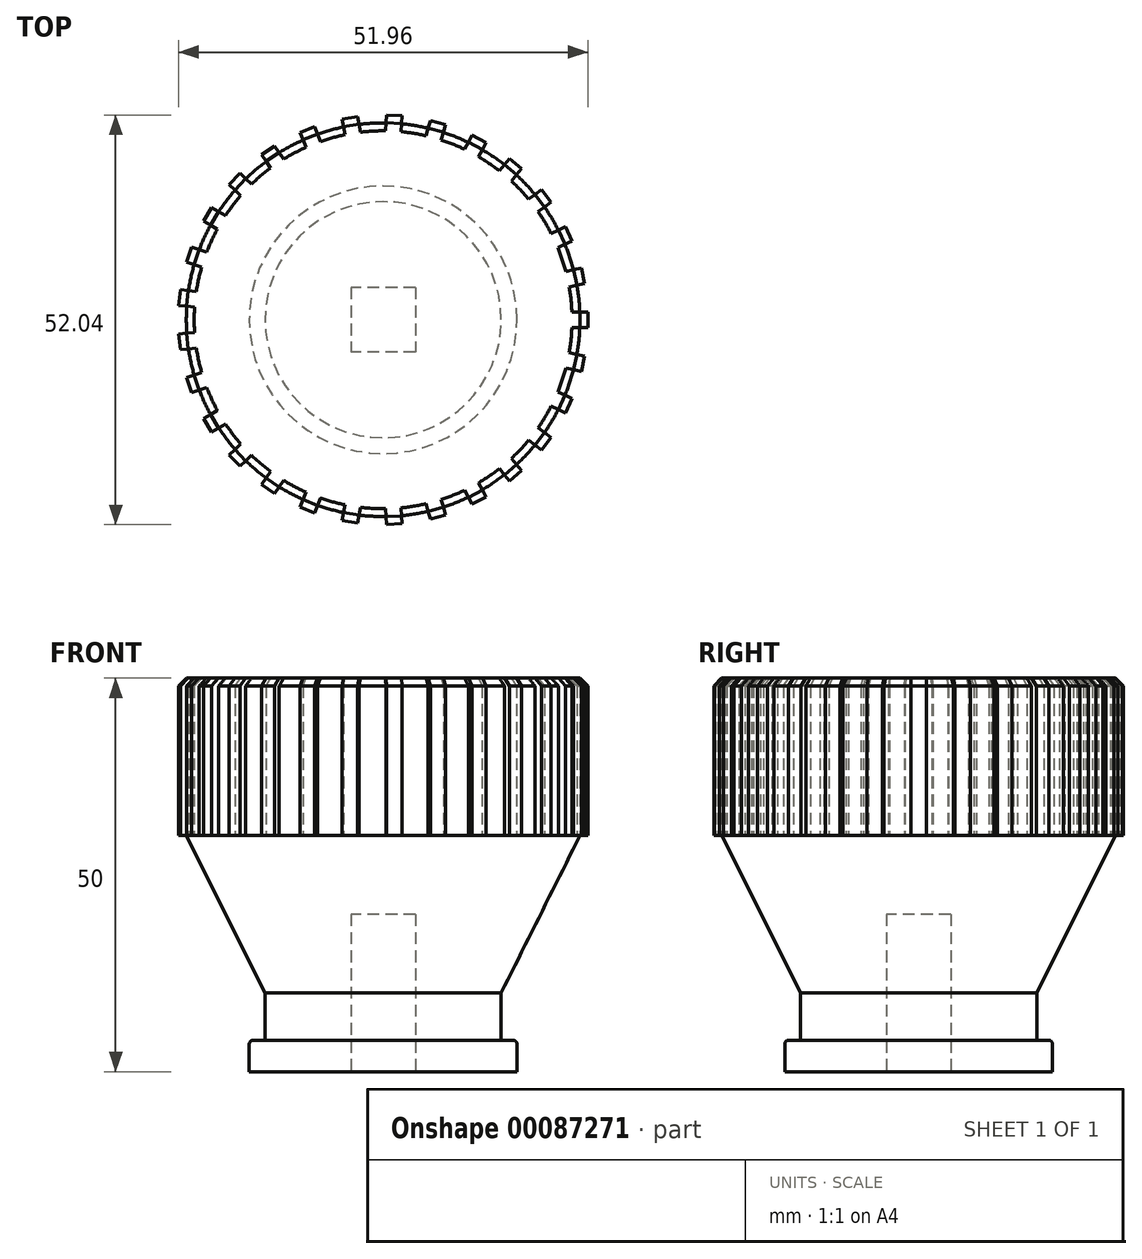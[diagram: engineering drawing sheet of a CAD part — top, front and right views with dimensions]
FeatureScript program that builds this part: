
annotation { "Feature Type Name" : "Feature", "Feature Type Description" : "" }
export const myFeature = defineFeature(function(context is Context, id is Id, definition is map)
    precondition{}
    {
        {
            var Q0;
            Q0=qCreatedBy(makeId("Top.planeOp"),FACE);
            var sketch = newSketch(context, id + "F0", { "sketchPlane" : qUnion([Q0])});
            skCircle(sketch, "E0", {"center": v(0, 0) * mm, "radius": 15 * mm});
            skLineSegment(sketch, "E1", {"start": v(0, 0) * mm, "end": v(0, 4.1) * mm, "construction": true});
            skLineSegment(sketch, "E2", {"start": v(0, 4.1) * mm, "end": v(4.1, 4.1) * mm, "construction": true});
            skLineSegment(sketch, "E3.bottom", {"start": v(4.1, 4.1) * mm, "end": v(-4.1, 4.1) * mm});
            skLineSegment(sketch, "E3.top", {"start": v(4.1, -4.1) * mm, "end": v(-4.1, -4.1) * mm});
            skLineSegment(sketch, "E3.left", {"start": v(4.1, 4.1) * mm, "end": v(4.1, -4.1) * mm});
            skLineSegment(sketch, "E3.right", {"start": v(-4.1, 4.1) * mm, "end": v(-4.1, -4.1) * mm});
            skSolve(sketch);
        }
        {
            var Q0;
            Q0=makeQuery(id+"F0.imprint","IMPRINT",FACE,{"disambiguationData":[TD([[makeQuery(id+"F0.imprint","IMPRINT",EDGE,{"derivedFrom":sQuery(id+"F0.wireOp",EDGE,"E0")}),1.0]])]});
            var Q1;
            Q1=makeQuery(id+"F0.imprint","IMPRINT",FACE,{"disambiguationData":[TD([[makeQuery(id+"F0.imprint","IMPRINT",EDGE,{"derivedFrom":sQuery(id+"F0.wireOp",EDGE,"E3.bottom")}),1.0]])]});
            extrude(context, id + "F1", {"entities" : qUnion([Q0, Q1]), "depth" : 10 * mm});
        }
        {
            var Q0;
            Q0=makeQuery(id+"F1.opExtrude","CAP_FACE",FACE,{"disambiguationData":[OSD([sQuery(id+"F0.wireOp",EDGE,"E0"),sQuery(id+"F0.wireOp",EDGE,"E3.bottom"),sQuery(id+"F0.wireOp",EDGE,"E3.top"),sQuery(id+"F0.wireOp",EDGE,"E3.left"),sQuery(id+"F0.wireOp",EDGE,"E3.right")])],"isStart":false});
            cPlane(context, id + "F2", {"entities" : qUnion([Q0]), "cplaneType" : CPlaneType.OFFSET, "offset" : 20 * mm, "width" : 150 * mm, "height" : 150 * mm});
        }
        {
            var Q0;
            Q0=qCreatedBy(id+"F2.planeOp",FACE);
            var sketch = newSketch(context, id + "F3", { "sketchPlane" : qUnion([Q0])});
            skCircle(sketch, "E4", {"center": v(0, 0) * mm, "radius": 25 * mm});
            skLineSegment(sketch, "E5", {"start": v(26, 0) * mm, "end": v(26, -1) * mm});
            skLineSegment(sketch, "E6", {"start": v(26, 0) * mm, "end": v(26, 1) * mm});
            skLineSegment(sketch, "E7", {"start": v(26, 1) * mm, "end": v(24.98, 1) * mm});
            skLineSegment(sketch, "E8", {"start": v(26, -1) * mm, "end": v(24.98, -1) * mm});
            skLineSegment(sketch, "E9.1.0", {"start": v(25.4, -5.59) * mm, "end": v(25.6, -4.61) * mm});
            skLineSegment(sketch, "E9.1.1", {"start": v(25.4, -5.59) * mm, "end": v(25.18, -6.57) * mm});
            skLineSegment(sketch, "E9.1.2", {"start": v(25.6, -4.61) * mm, "end": v(24.61, -4.4) * mm});
            skLineSegment(sketch, "E9.1.3", {"start": v(25.18, -6.57) * mm, "end": v(24.18, -6.35) * mm});
            skLineSegment(sketch, "E9.2.0", {"start": v(23.6, -10.92) * mm, "end": v(24.02, -10) * mm});
            skLineSegment(sketch, "E9.2.1", {"start": v(23.6, -10.92) * mm, "end": v(23.18, -11.82) * mm});
            skLineSegment(sketch, "E9.2.2", {"start": v(24.02, -10) * mm, "end": v(23.1, -9.58) * mm});
            skLineSegment(sketch, "E9.2.3", {"start": v(23.18, -11.82) * mm, "end": v(22.25, -11.4) * mm});
            skLineSegment(sketch, "E9.3.0", {"start": v(20.7, -15.73) * mm, "end": v(21.3, -14.94) * mm});
            skLineSegment(sketch, "E9.3.1", {"start": v(20.7, -15.73) * mm, "end": v(20.1, -16.53) * mm});
            skLineSegment(sketch, "E9.3.2", {"start": v(21.3, -14.94) * mm, "end": v(20.5, -14.32) * mm});
            skLineSegment(sketch, "E9.3.3", {"start": v(20.1, -16.53) * mm, "end": v(19.28, -15.91) * mm});
            skLineSegment(sketch, "E9.4.0", {"start": v(16.83, -19.82) * mm, "end": v(17.6, -19.17) * mm});
            skLineSegment(sketch, "E9.4.1", {"start": v(16.83, -19.82) * mm, "end": v(16.07, -20.46) * mm});
            skLineSegment(sketch, "E9.4.2", {"start": v(17.6, -19.17) * mm, "end": v(16.93, -18.4) * mm});
            skLineSegment(sketch, "E9.4.3", {"start": v(16.07, -20.46) * mm, "end": v(15.4, -19.69) * mm});
            skLineSegment(sketch, "E9.5.0", {"start": v(12.18, -22.97) * mm, "end": v(13.06, -22.5) * mm});
            skLineSegment(sketch, "E9.5.1", {"start": v(12.18, -22.97) * mm, "end": v(11.3, -23.44) * mm});
            skLineSegment(sketch, "E9.5.2", {"start": v(13.06, -22.5) * mm, "end": v(12.58, -21.6) * mm});
            skLineSegment(sketch, "E9.5.3", {"start": v(11.3, -23.44) * mm, "end": v(10.82, -22.54) * mm});
            skLineSegment(sketch, "E9.6.0", {"start": v(6.96, -25.05) * mm, "end": v(7.92, -24.78) * mm});
            skLineSegment(sketch, "E9.6.1", {"start": v(6.96, -25.05) * mm, "end": v(6, -25.32) * mm});
            skLineSegment(sketch, "E9.6.2", {"start": v(7.92, -24.78) * mm, "end": v(7.65, -23.8) * mm});
            skLineSegment(sketch, "E9.6.3", {"start": v(6, -25.32) * mm, "end": v(5.72, -24.34) * mm});
            skLineSegment(sketch, "E9.7.0", {"start": v(1.4, -25.96) * mm, "end": v(2.4, -25.9) * mm});
            skLineSegment(sketch, "E9.7.1", {"start": v(1.4, -25.96) * mm, "end": v(0.4, -26.02) * mm});
            skLineSegment(sketch, "E9.7.2", {"start": v(2.4, -25.9) * mm, "end": v(2.35, -24.89) * mm});
            skLineSegment(sketch, "E9.7.3", {"start": v(0.4, -26.02) * mm, "end": v(0.35, -25) * mm});
            skLineSegment(sketch, "E9.8.0", {"start": v(-4.2, -25.66) * mm, "end": v(-3.22, -25.82) * mm});
            skLineSegment(sketch, "E9.8.1", {"start": v(-4.2, -25.66) * mm, "end": v(-5.2, -25.5) * mm});
            skLineSegment(sketch, "E9.8.2", {"start": v(-3.22, -25.82) * mm, "end": v(-3.05, -24.81) * mm});
            skLineSegment(sketch, "E9.8.3", {"start": v(-5.2, -25.5) * mm, "end": v(-5.03, -24.49) * mm});
            skLineSegment(sketch, "E9.9.0", {"start": v(-9.62, -24.15) * mm, "end": v(-8.7, -24.52) * mm});
            skLineSegment(sketch, "E9.9.1", {"start": v(-9.62, -24.15) * mm, "end": v(-10.55, -23.78) * mm});
            skLineSegment(sketch, "E9.9.2", {"start": v(-8.7, -24.52) * mm, "end": v(-8.32, -23.58) * mm});
            skLineSegment(sketch, "E9.9.3", {"start": v(-10.55, -23.78) * mm, "end": v(-10.18, -22.84) * mm});
            skLineSegment(sketch, "E9.10.0", {"start": v(-14.6, -21.52) * mm, "end": v(-13.76, -22.08) * mm});
            skLineSegment(sketch, "E9.10.1", {"start": v(-14.6, -21.52) * mm, "end": v(-15.42, -20.96) * mm});
            skLineSegment(sketch, "E9.10.2", {"start": v(-13.76, -22.08) * mm, "end": v(-13.2, -21.24) * mm});
            skLineSegment(sketch, "E9.10.3", {"start": v(-15.42, -20.96) * mm, "end": v(-14.85, -20.11) * mm});
            skLineSegment(sketch, "E9.11.0", {"start": v(-18.88, -17.88) * mm, "end": v(-18.19, -18.6) * mm});
            skLineSegment(sketch, "E9.11.1", {"start": v(-18.88, -17.88) * mm, "end": v(-19.56, -17.15) * mm});
            skLineSegment(sketch, "E9.11.2", {"start": v(-18.19, -18.6) * mm, "end": v(-17.45, -17.9) * mm});
            skLineSegment(sketch, "E9.11.3", {"start": v(-19.56, -17.15) * mm, "end": v(-18.82, -16.45) * mm});
            skLineSegment(sketch, "E9.12.0", {"start": v(-22.28, -13.4) * mm, "end": v(-21.76, -14.26) * mm});
            skLineSegment(sketch, "E9.12.1", {"start": v(-22.28, -13.4) * mm, "end": v(-22.8, -12.55) * mm});
            skLineSegment(sketch, "E9.12.2", {"start": v(-21.76, -14.26) * mm, "end": v(-20.89, -13.74) * mm});
            skLineSegment(sketch, "E9.12.3", {"start": v(-22.8, -12.55) * mm, "end": v(-21.92, -12.02) * mm});
            skLineSegment(sketch, "E9.13.0", {"start": v(-24.64, -8.3) * mm, "end": v(-24.32, -9.25) * mm});
            skLineSegment(sketch, "E9.13.1", {"start": v(-24.64, -8.3) * mm, "end": v(-24.96, -7.35) * mm});
            skLineSegment(sketch, "E9.13.2", {"start": v(-24.32, -9.25) * mm, "end": v(-23.35, -8.92) * mm});
            skLineSegment(sketch, "E9.13.3", {"start": v(-24.96, -7.35) * mm, "end": v(-24, -7.03) * mm});
            skLineSegment(sketch, "E9.14.0", {"start": v(-25.85, -2.81) * mm, "end": v(-25.74, -3.8) * mm});
            skLineSegment(sketch, "E9.14.1", {"start": v(-25.85, -2.81) * mm, "end": v(-25.96, -1.82) * mm});
            skLineSegment(sketch, "E9.14.2", {"start": v(-25.74, -3.8) * mm, "end": v(-24.73, -3.7) * mm});
            skLineSegment(sketch, "E9.14.3", {"start": v(-25.96, -1.82) * mm, "end": v(-24.94, -1.7) * mm});
            skLineSegment(sketch, "E9.15.0", {"start": v(-25.85, 2.81) * mm, "end": v(-25.96, 1.82) * mm});
            skLineSegment(sketch, "E9.15.1", {"start": v(-25.85, 2.81) * mm, "end": v(-25.74, 3.8) * mm});
            skLineSegment(sketch, "E9.15.2", {"start": v(-25.96, 1.82) * mm, "end": v(-24.94, 1.7) * mm});
            skLineSegment(sketch, "E9.15.3", {"start": v(-25.74, 3.8) * mm, "end": v(-24.73, 3.7) * mm});
            skLineSegment(sketch, "E9.16.0", {"start": v(-24.64, 8.3) * mm, "end": v(-24.96, 7.35) * mm});
            skLineSegment(sketch, "E9.16.1", {"start": v(-24.64, 8.3) * mm, "end": v(-24.32, 9.25) * mm});
            skLineSegment(sketch, "E9.16.2", {"start": v(-24.96, 7.35) * mm, "end": v(-24, 7.03) * mm});
            skLineSegment(sketch, "E9.16.3", {"start": v(-24.32, 9.25) * mm, "end": v(-23.35, 8.92) * mm});
            skLineSegment(sketch, "E9.17.0", {"start": v(-22.28, 13.4) * mm, "end": v(-22.8, 12.55) * mm});
            skLineSegment(sketch, "E9.17.1", {"start": v(-22.28, 13.4) * mm, "end": v(-21.76, 14.26) * mm});
            skLineSegment(sketch, "E9.17.2", {"start": v(-22.8, 12.55) * mm, "end": v(-21.92, 12.02) * mm});
            skLineSegment(sketch, "E9.17.3", {"start": v(-21.76, 14.26) * mm, "end": v(-20.89, 13.74) * mm});
            skLineSegment(sketch, "E9.18.0", {"start": v(-18.88, 17.88) * mm, "end": v(-19.56, 17.15) * mm});
            skLineSegment(sketch, "E9.18.1", {"start": v(-18.88, 17.88) * mm, "end": v(-18.19, 18.6) * mm});
            skLineSegment(sketch, "E9.18.2", {"start": v(-19.56, 17.15) * mm, "end": v(-18.82, 16.45) * mm});
            skLineSegment(sketch, "E9.18.3", {"start": v(-18.19, 18.6) * mm, "end": v(-17.45, 17.9) * mm});
            skLineSegment(sketch, "E9.19.0", {"start": v(-14.6, 21.52) * mm, "end": v(-15.42, 20.96) * mm});
            skLineSegment(sketch, "E9.19.1", {"start": v(-14.6, 21.52) * mm, "end": v(-13.76, 22.08) * mm});
            skLineSegment(sketch, "E9.19.2", {"start": v(-15.42, 20.96) * mm, "end": v(-14.85, 20.11) * mm});
            skLineSegment(sketch, "E9.19.3", {"start": v(-13.76, 22.08) * mm, "end": v(-13.2, 21.24) * mm});
            skLineSegment(sketch, "E9.20.0", {"start": v(-9.62, 24.15) * mm, "end": v(-10.55, 23.78) * mm});
            skLineSegment(sketch, "E9.20.1", {"start": v(-9.62, 24.15) * mm, "end": v(-8.7, 24.52) * mm});
            skLineSegment(sketch, "E9.20.2", {"start": v(-10.55, 23.78) * mm, "end": v(-10.18, 22.84) * mm});
            skLineSegment(sketch, "E9.20.3", {"start": v(-8.7, 24.52) * mm, "end": v(-8.32, 23.58) * mm});
            skLineSegment(sketch, "E9.21.0", {"start": v(-4.2, 25.66) * mm, "end": v(-5.2, 25.5) * mm});
            skLineSegment(sketch, "E9.21.1", {"start": v(-4.2, 25.66) * mm, "end": v(-3.22, 25.82) * mm});
            skLineSegment(sketch, "E9.21.2", {"start": v(-5.2, 25.5) * mm, "end": v(-5.03, 24.49) * mm});
            skLineSegment(sketch, "E9.21.3", {"start": v(-3.22, 25.82) * mm, "end": v(-3.05, 24.81) * mm});
            skLineSegment(sketch, "E9.22.0", {"start": v(1.4, 25.96) * mm, "end": v(0.4, 26.02) * mm});
            skLineSegment(sketch, "E9.22.1", {"start": v(1.4, 25.96) * mm, "end": v(2.4, 25.9) * mm});
            skLineSegment(sketch, "E9.22.2", {"start": v(0.4, 26.02) * mm, "end": v(0.35, 25) * mm});
            skLineSegment(sketch, "E9.22.3", {"start": v(2.4, 25.9) * mm, "end": v(2.35, 24.89) * mm});
            skLineSegment(sketch, "E9.23.0", {"start": v(6.96, 25.05) * mm, "end": v(6, 25.32) * mm});
            skLineSegment(sketch, "E9.23.1", {"start": v(6.96, 25.05) * mm, "end": v(7.92, 24.78) * mm});
            skLineSegment(sketch, "E9.23.2", {"start": v(6, 25.32) * mm, "end": v(5.72, 24.34) * mm});
            skLineSegment(sketch, "E9.23.3", {"start": v(7.92, 24.78) * mm, "end": v(7.65, 23.8) * mm});
            skLineSegment(sketch, "E9.24.0", {"start": v(12.18, 22.97) * mm, "end": v(11.3, 23.44) * mm});
            skLineSegment(sketch, "E9.24.1", {"start": v(12.18, 22.97) * mm, "end": v(13.06, 22.5) * mm});
            skLineSegment(sketch, "E9.24.2", {"start": v(11.3, 23.44) * mm, "end": v(10.82, 22.54) * mm});
            skLineSegment(sketch, "E9.24.3", {"start": v(13.06, 22.5) * mm, "end": v(12.58, 21.6) * mm});
            skLineSegment(sketch, "E9.25.0", {"start": v(16.83, 19.82) * mm, "end": v(16.07, 20.46) * mm});
            skLineSegment(sketch, "E9.25.1", {"start": v(16.83, 19.82) * mm, "end": v(17.6, 19.17) * mm});
            skLineSegment(sketch, "E9.25.2", {"start": v(16.07, 20.46) * mm, "end": v(15.4, 19.69) * mm});
            skLineSegment(sketch, "E9.25.3", {"start": v(17.6, 19.17) * mm, "end": v(16.93, 18.4) * mm});
            skLineSegment(sketch, "E9.26.0", {"start": v(20.7, 15.73) * mm, "end": v(20.1, 16.53) * mm});
            skLineSegment(sketch, "E9.26.1", {"start": v(20.7, 15.73) * mm, "end": v(21.3, 14.94) * mm});
            skLineSegment(sketch, "E9.26.2", {"start": v(20.1, 16.53) * mm, "end": v(19.28, 15.91) * mm});
            skLineSegment(sketch, "E9.26.3", {"start": v(21.3, 14.94) * mm, "end": v(20.5, 14.32) * mm});
            skLineSegment(sketch, "E9.27.0", {"start": v(23.6, 10.92) * mm, "end": v(23.18, 11.82) * mm});
            skLineSegment(sketch, "E9.27.1", {"start": v(23.6, 10.92) * mm, "end": v(24.02, 10) * mm});
            skLineSegment(sketch, "E9.27.2", {"start": v(23.18, 11.82) * mm, "end": v(22.25, 11.4) * mm});
            skLineSegment(sketch, "E9.27.3", {"start": v(24.02, 10) * mm, "end": v(23.1, 9.58) * mm});
            skLineSegment(sketch, "E9.28.0", {"start": v(25.4, 5.59) * mm, "end": v(25.18, 6.57) * mm});
            skLineSegment(sketch, "E9.28.1", {"start": v(25.4, 5.59) * mm, "end": v(25.6, 4.61) * mm});
            skLineSegment(sketch, "E9.28.2", {"start": v(25.18, 6.57) * mm, "end": v(24.18, 6.35) * mm});
            skLineSegment(sketch, "E9.28.3", {"start": v(25.6, 4.61) * mm, "end": v(24.61, 4.4) * mm});
            skLineSegment(sketch, "E9.anchor1", {"start": v(0, 0) * mm, "end": v(26, 0) * mm, "construction": true});
            skLineSegment(sketch, "E9.anchor2", {"start": v(0, 0) * mm, "end": v(26, 0) * mm, "construction": true});
            skSolve(sketch);
        }
        {
            var Q1;
            Q1=makeQuery(id+"F1.opExtrude","CAP_FACE",FACE,{"disambiguationData":[OSD([sQuery(id+"F0.wireOp",EDGE,"E0")])],"isStart":false});
            var Q2;
            Q2=makeQuery(id+"F3.imprint","IMPRINT",FACE,{"disambiguationData":[TD([[makeQuery(id+"F3.imprint","IMPRINT",EDGE,{"derivedFrom":sQuery(id+"F3.wireOp",EDGE,"E4")}),1.0]])]});
            loft(context, id + "F4", {"operationType" : NewBodyOperationType.ADD, "sheetProfilesArray" : [{ "sheetProfileEntities" : qUnion([Q1]) }, { "sheetProfileEntities" : qUnion([Q2]) }]});
        }
        {
            var Q0;
            Q0 = qSketchRegion(id + "F3", true);
            extrude(context, id + "F5", {"entities" : qUnion([Q0]), "operationType" : NewBodyOperationType.ADD, "depth" : 20 * mm});
        }
        {
            var Q0;
            Q0=makeQuery(id+"F0.imprint","IMPRINT",FACE,{"disambiguationData":[TD([[makeQuery(id+"F0.imprint","IMPRINT",EDGE,{"derivedFrom":sQuery(id+"F0.wireOp",EDGE,"E3.bottom")}),1.0]])]});
            extrude(context, id + "F6", {"entities" : qUnion([Q0]), "operationType" : NewBodyOperationType.REMOVE, "depth" : 20 * mm});
        }
        {
            var Q0;
            {var subQ0=sQuery(id+"F3.wireOp",EDGE,"E4");Q0=makeQuery(id+"F5.opExtrude","CAP_EDGE",EDGE,{"disambiguationData":[OSD([subQ0]),TDD([makeQuery(id+"F3.imprint","IMPRINT",EDGE,{"disambiguationData":[TD([[makeQuery(id+"F3.imprint","INTERSECT",VERTEX,{"derivedFrom":[subQ0,sQuery(id+"F3.wireOp",EDGE,"E9.5.3")]}),1.0]])],"derivedFrom":subQ0})])],"isStart":false});}
            var Q1;
            Q1=makeQuery(id+"F5.opExtrude","CAP_EDGE",EDGE,{"disambiguationData":[OSD([sQuery(id+"F3.wireOp",EDGE,"E9.6.0"),sQuery(id+"F3.wireOp",EDGE,"E9.6.1")])],"isStart":false});
            var Q2;
            {var subQ0=sQuery(id+"F3.wireOp",EDGE,"E4");Q2=makeQuery(id+"F5.opExtrude","CAP_EDGE",EDGE,{"disambiguationData":[OSD([subQ0]),TDD([makeQuery(id+"F3.imprint","IMPRINT",EDGE,{"disambiguationData":[TD([[makeQuery(id+"F3.imprint","INTERSECT",VERTEX,{"derivedFrom":[subQ0,sQuery(id+"F3.wireOp",EDGE,"E9.6.3")]}),1.0]])],"derivedFrom":subQ0})])],"isStart":false});}
            var Q3;
            {var subQ0=sQuery(id+"F3.wireOp",EDGE,"E4");Q3=makeQuery(id+"F5.opExtrude","CAP_EDGE",EDGE,{"disambiguationData":[OSD([subQ0]),TDD([makeQuery(id+"F3.imprint","IMPRINT",EDGE,{"disambiguationData":[TD([[makeQuery(id+"F3.imprint","INTERSECT",VERTEX,{"derivedFrom":[subQ0,sQuery(id+"F3.wireOp",EDGE,"E9.7.3")]}),1.0]])],"derivedFrom":subQ0})])],"isStart":false});}
            var Q4;
            Q4=makeQuery(id+"F5.opExtrude","CAP_EDGE",EDGE,{"disambiguationData":[OSD([sQuery(id+"F3.wireOp",EDGE,"E9.7.0"),sQuery(id+"F3.wireOp",EDGE,"E9.7.1")])],"isStart":false});
            var Q5;
            Q5=makeQuery(id+"F5.opExtrude","CAP_EDGE",EDGE,{"disambiguationData":[OSD([sQuery(id+"F3.wireOp",EDGE,"E9.5.0"),sQuery(id+"F3.wireOp",EDGE,"E9.5.1")])],"isStart":false});
            var Q6;
            {var subQ0=sQuery(id+"F3.wireOp",EDGE,"E4");Q6=makeQuery(id+"F5.opExtrude","CAP_EDGE",EDGE,{"disambiguationData":[OSD([subQ0]),TDD([makeQuery(id+"F3.imprint","IMPRINT",EDGE,{"disambiguationData":[TD([[makeQuery(id+"F3.imprint","INTERSECT",VERTEX,{"derivedFrom":[subQ0,sQuery(id+"F3.wireOp",EDGE,"E9.4.3")]}),1.0]])],"derivedFrom":subQ0})])],"isStart":false});}
            var Q7;
            Q7=makeQuery(id+"F5.opExtrude","CAP_EDGE",EDGE,{"disambiguationData":[OSD([sQuery(id+"F3.wireOp",EDGE,"E9.4.0"),sQuery(id+"F3.wireOp",EDGE,"E9.4.1")])],"isStart":false});
            var Q8;
            {var subQ0=sQuery(id+"F3.wireOp",EDGE,"E4");Q8=makeQuery(id+"F5.opExtrude","CAP_EDGE",EDGE,{"disambiguationData":[OSD([subQ0]),TDD([makeQuery(id+"F3.imprint","IMPRINT",EDGE,{"disambiguationData":[TD([[makeQuery(id+"F3.imprint","INTERSECT",VERTEX,{"derivedFrom":[subQ0,sQuery(id+"F3.wireOp",EDGE,"E9.3.3")]}),1.0]])],"derivedFrom":subQ0})])],"isStart":false});}
            var Q9;
            Q9=makeQuery(id+"F5.opExtrude","CAP_EDGE",EDGE,{"disambiguationData":[OSD([sQuery(id+"F3.wireOp",EDGE,"E9.3.0"),sQuery(id+"F3.wireOp",EDGE,"E9.3.1")])],"isStart":false});
            var Q10;
            Q10=makeQuery(id+"F5.opExtrude","CAP_EDGE",EDGE,{"disambiguationData":[OSD([sQuery(id+"F3.wireOp",EDGE,"E9.8.0"),sQuery(id+"F3.wireOp",EDGE,"E9.8.1")])],"isStart":false});
            var Q11;
            {var subQ0=sQuery(id+"F3.wireOp",EDGE,"E4");Q11=makeQuery(id+"F5.opExtrude","CAP_EDGE",EDGE,{"disambiguationData":[OSD([subQ0]),TDD([makeQuery(id+"F3.imprint","IMPRINT",EDGE,{"disambiguationData":[TD([[makeQuery(id+"F3.imprint","INTERSECT",VERTEX,{"derivedFrom":[subQ0,sQuery(id+"F3.wireOp",EDGE,"E9.8.3")]}),1.0]])],"derivedFrom":subQ0})])],"isStart":false});}
            var Q12;
            Q12=makeQuery(id+"F5.opExtrude","CAP_EDGE",EDGE,{"disambiguationData":[OSD([sQuery(id+"F3.wireOp",EDGE,"E9.9.0"),sQuery(id+"F3.wireOp",EDGE,"E9.9.1")])],"isStart":false});
            var Q13;
            {var subQ0=sQuery(id+"F3.wireOp",EDGE,"E4");Q13=makeQuery(id+"F5.opExtrude","CAP_EDGE",EDGE,{"disambiguationData":[OSD([subQ0]),TDD([makeQuery(id+"F3.imprint","IMPRINT",EDGE,{"disambiguationData":[TD([[makeQuery(id+"F3.imprint","INTERSECT",VERTEX,{"derivedFrom":[subQ0,sQuery(id+"F3.wireOp",EDGE,"E9.9.3")]}),1.0]])],"derivedFrom":subQ0})])],"isStart":false});}
            var Q14;
            Q14=makeQuery(id+"F5.opExtrude","CAP_EDGE",EDGE,{"disambiguationData":[OSD([sQuery(id+"F3.wireOp",EDGE,"E9.10.0"),sQuery(id+"F3.wireOp",EDGE,"E9.10.1")])],"isStart":false});
            var Q15;
            {var subQ0=sQuery(id+"F3.wireOp",EDGE,"E4");Q15=makeQuery(id+"F5.opExtrude","CAP_EDGE",EDGE,{"disambiguationData":[OSD([subQ0]),TDD([makeQuery(id+"F3.imprint","IMPRINT",EDGE,{"disambiguationData":[TD([[makeQuery(id+"F3.imprint","INTERSECT",VERTEX,{"derivedFrom":[subQ0,sQuery(id+"F3.wireOp",EDGE,"E9.10.3")]}),1.0]])],"derivedFrom":subQ0})])],"isStart":false});}
            var Q16;
            Q16=makeQuery(id+"F5.opExtrude","CAP_EDGE",EDGE,{"disambiguationData":[OSD([sQuery(id+"F3.wireOp",EDGE,"E9.11.0"),sQuery(id+"F3.wireOp",EDGE,"E9.11.1")])],"isStart":false});
            var Q17;
            {var subQ0=sQuery(id+"F3.wireOp",EDGE,"E4");Q17=makeQuery(id+"F5.opExtrude","CAP_EDGE",EDGE,{"disambiguationData":[OSD([subQ0]),TDD([makeQuery(id+"F3.imprint","IMPRINT",EDGE,{"disambiguationData":[TD([[makeQuery(id+"F3.imprint","INTERSECT",VERTEX,{"derivedFrom":[subQ0,sQuery(id+"F3.wireOp",EDGE,"E9.11.3")]}),1.0]])],"derivedFrom":subQ0})])],"isStart":false});}
            var Q18;
            {var subQ0=sQuery(id+"F3.wireOp",EDGE,"E4");Q18=makeQuery(id+"F5.opExtrude","CAP_EDGE",EDGE,{"disambiguationData":[OSD([subQ0]),TDD([makeQuery(id+"F3.imprint","IMPRINT",EDGE,{"disambiguationData":[TD([[makeQuery(id+"F3.imprint","INTERSECT",VERTEX,{"derivedFrom":[subQ0,sQuery(id+"F3.wireOp",EDGE,"E9.2.3")]}),1.0]])],"derivedFrom":subQ0})])],"isStart":false});}
            var Q19;
            {var subQ0=sQuery(id+"F3.wireOp",EDGE,"E4");Q19=makeQuery(id+"F5.opExtrude","CAP_EDGE",EDGE,{"disambiguationData":[OSD([subQ0]),TDD([makeQuery(id+"F3.imprint","IMPRINT",EDGE,{"disambiguationData":[TD([[makeQuery(id+"F3.imprint","INTERSECT",VERTEX,{"derivedFrom":[subQ0,sQuery(id+"F3.wireOp",EDGE,"E9.1.3")]}),1.0]])],"derivedFrom":subQ0})])],"isStart":false});}
            var Q20;
            Q20=makeQuery(id+"F5.opExtrude","CAP_EDGE",EDGE,{"disambiguationData":[OSD([sQuery(id+"F3.wireOp",EDGE,"E9.2.0"),sQuery(id+"F3.wireOp",EDGE,"E9.2.1")])],"isStart":false});
            var Q21;
            Q21=makeQuery(id+"F5.opExtrude","CAP_EDGE",EDGE,{"disambiguationData":[OSD([sQuery(id+"F3.wireOp",EDGE,"E9.1.0"),sQuery(id+"F3.wireOp",EDGE,"E9.1.1")])],"isStart":false});
            var Q22;
            {var subQ0=sQuery(id+"F3.wireOp",EDGE,"E4");Q22=makeQuery(id+"F5.opExtrude","CAP_EDGE",EDGE,{"disambiguationData":[OSD([subQ0]),TDD([makeQuery(id+"F3.imprint","IMPRINT",EDGE,{"disambiguationData":[TD([[makeQuery(id+"F3.imprint","INTERSECT",VERTEX,{"derivedFrom":[subQ0,sQuery(id+"F3.wireOp",EDGE,"E9.1.2")]}),-1.0]])],"derivedFrom":subQ0})])],"isStart":false});}
            var Q23;
            Q23=makeQuery(id+"F5.opExtrude","CAP_EDGE",EDGE,{"disambiguationData":[OSD([sQuery(id+"F3.wireOp",EDGE,"E9.12.0"),sQuery(id+"F3.wireOp",EDGE,"E9.12.1")])],"isStart":false});
            var Q24;
            {var subQ0=sQuery(id+"F3.wireOp",EDGE,"E4");Q24=makeQuery(id+"F5.opExtrude","CAP_EDGE",EDGE,{"disambiguationData":[OSD([subQ0]),TDD([makeQuery(id+"F3.imprint","IMPRINT",EDGE,{"disambiguationData":[TD([[makeQuery(id+"F3.imprint","INTERSECT",VERTEX,{"derivedFrom":[subQ0,sQuery(id+"F3.wireOp",EDGE,"E9.12.3")]}),1.0]])],"derivedFrom":subQ0})])],"isStart":false});}
            var Q25;
            Q25=makeQuery(id+"F5.opExtrude","CAP_EDGE",EDGE,{"disambiguationData":[OSD([sQuery(id+"F3.wireOp",EDGE,"E6"),sQuery(id+"F3.wireOp",EDGE,"E5")])],"isStart":false});
            var Q26;
            {var subQ0=sQuery(id+"F3.wireOp",EDGE,"E4");Q26=makeQuery(id+"F5.opExtrude","CAP_EDGE",EDGE,{"disambiguationData":[OSD([subQ0]),TDD([makeQuery(id+"F3.imprint","IMPRINT",EDGE,{"disambiguationData":[TD([[makeQuery(id+"F3.imprint","INTERSECT",VERTEX,{"derivedFrom":[subQ0,sQuery(id+"F3.wireOp",EDGE,"E9.28.3")]}),1.0]])],"derivedFrom":subQ0})])],"isStart":false});}
            var Q27;
            Q27=makeQuery(id+"F5.opExtrude","CAP_EDGE",EDGE,{"disambiguationData":[OSD([sQuery(id+"F3.wireOp",EDGE,"E9.28.0"),sQuery(id+"F3.wireOp",EDGE,"E9.28.1")])],"isStart":false});
            var Q28;
            {var subQ0=sQuery(id+"F3.wireOp",EDGE,"E4");Q28=makeQuery(id+"F5.opExtrude","CAP_EDGE",EDGE,{"disambiguationData":[OSD([subQ0]),TDD([makeQuery(id+"F3.imprint","IMPRINT",EDGE,{"disambiguationData":[TD([[makeQuery(id+"F3.imprint","INTERSECT",VERTEX,{"derivedFrom":[subQ0,sQuery(id+"F3.wireOp",EDGE,"E9.27.3")]}),1.0]])],"derivedFrom":subQ0})])],"isStart":false});}
            var Q29;
            Q29=makeQuery(id+"F5.opExtrude","CAP_EDGE",EDGE,{"disambiguationData":[OSD([sQuery(id+"F3.wireOp",EDGE,"E9.27.0"),sQuery(id+"F3.wireOp",EDGE,"E9.27.1")])],"isStart":false});
            var Q30;
            {var subQ0=sQuery(id+"F3.wireOp",EDGE,"E4");Q30=makeQuery(id+"F5.opExtrude","CAP_EDGE",EDGE,{"disambiguationData":[OSD([subQ0]),TDD([makeQuery(id+"F3.imprint","IMPRINT",EDGE,{"disambiguationData":[TD([[makeQuery(id+"F3.imprint","INTERSECT",VERTEX,{"derivedFrom":[subQ0,sQuery(id+"F3.wireOp",EDGE,"E9.26.3")]}),1.0]])],"derivedFrom":subQ0})])],"isStart":false});}
            var Q31;
            Q31=makeQuery(id+"F5.opExtrude","CAP_EDGE",EDGE,{"disambiguationData":[OSD([sQuery(id+"F3.wireOp",EDGE,"E9.26.0"),sQuery(id+"F3.wireOp",EDGE,"E9.26.1")])],"isStart":false});
            var Q32;
            {var subQ0=sQuery(id+"F3.wireOp",EDGE,"E4");Q32=makeQuery(id+"F5.opExtrude","CAP_EDGE",EDGE,{"disambiguationData":[OSD([subQ0]),TDD([makeQuery(id+"F3.imprint","IMPRINT",EDGE,{"disambiguationData":[TD([[makeQuery(id+"F3.imprint","INTERSECT",VERTEX,{"derivedFrom":[subQ0,sQuery(id+"F3.wireOp",EDGE,"E9.25.3")]}),1.0]])],"derivedFrom":subQ0})])],"isStart":false});}
            var Q33;
            Q33=makeQuery(id+"F5.opExtrude","CAP_EDGE",EDGE,{"disambiguationData":[OSD([sQuery(id+"F3.wireOp",EDGE,"E9.25.0"),sQuery(id+"F3.wireOp",EDGE,"E9.25.1")])],"isStart":false});
            var Q34;
            {var subQ0=sQuery(id+"F3.wireOp",EDGE,"E4");Q34=makeQuery(id+"F5.opExtrude","CAP_EDGE",EDGE,{"disambiguationData":[OSD([subQ0]),TDD([makeQuery(id+"F3.imprint","IMPRINT",EDGE,{"disambiguationData":[TD([[makeQuery(id+"F3.imprint","INTERSECT",VERTEX,{"derivedFrom":[subQ0,sQuery(id+"F3.wireOp",EDGE,"E9.24.3")]}),1.0]])],"derivedFrom":subQ0})])],"isStart":false});}
            var Q35;
            Q35=makeQuery(id+"F5.opExtrude","CAP_EDGE",EDGE,{"disambiguationData":[OSD([sQuery(id+"F3.wireOp",EDGE,"E9.24.0"),sQuery(id+"F3.wireOp",EDGE,"E9.24.1")])],"isStart":false});
            var Q36;
            {var subQ0=sQuery(id+"F3.wireOp",EDGE,"E4");Q36=makeQuery(id+"F5.opExtrude","CAP_EDGE",EDGE,{"disambiguationData":[OSD([subQ0]),TDD([makeQuery(id+"F3.imprint","IMPRINT",EDGE,{"disambiguationData":[TD([[makeQuery(id+"F3.imprint","INTERSECT",VERTEX,{"derivedFrom":[subQ0,sQuery(id+"F3.wireOp",EDGE,"E9.23.3")]}),1.0]])],"derivedFrom":subQ0})])],"isStart":false});}
            var Q37;
            Q37=makeQuery(id+"F5.opExtrude","CAP_EDGE",EDGE,{"disambiguationData":[OSD([sQuery(id+"F3.wireOp",EDGE,"E9.23.0"),sQuery(id+"F3.wireOp",EDGE,"E9.23.1")])],"isStart":false});
            var Q38;
            {var subQ0=sQuery(id+"F3.wireOp",EDGE,"E4");Q38=makeQuery(id+"F5.opExtrude","CAP_EDGE",EDGE,{"disambiguationData":[OSD([subQ0]),TDD([makeQuery(id+"F3.imprint","IMPRINT",EDGE,{"disambiguationData":[TD([[makeQuery(id+"F3.imprint","INTERSECT",VERTEX,{"derivedFrom":[subQ0,sQuery(id+"F3.wireOp",EDGE,"E9.22.3")]}),1.0]])],"derivedFrom":subQ0})])],"isStart":false});}
            var Q39;
            Q39=makeQuery(id+"F5.opExtrude","CAP_EDGE",EDGE,{"disambiguationData":[OSD([sQuery(id+"F3.wireOp",EDGE,"E9.22.0"),sQuery(id+"F3.wireOp",EDGE,"E9.22.1")])],"isStart":false});
            var Q40;
            {var subQ0=sQuery(id+"F3.wireOp",EDGE,"E4");Q40=makeQuery(id+"F5.opExtrude","CAP_EDGE",EDGE,{"disambiguationData":[OSD([subQ0]),TDD([makeQuery(id+"F3.imprint","IMPRINT",EDGE,{"disambiguationData":[TD([[makeQuery(id+"F3.imprint","INTERSECT",VERTEX,{"derivedFrom":[subQ0,sQuery(id+"F3.wireOp",EDGE,"E9.21.3")]}),1.0]])],"derivedFrom":subQ0})])],"isStart":false});}
            var Q41;
            Q41=makeQuery(id+"F5.opExtrude","CAP_EDGE",EDGE,{"disambiguationData":[OSD([sQuery(id+"F3.wireOp",EDGE,"E9.21.0"),sQuery(id+"F3.wireOp",EDGE,"E9.21.1")])],"isStart":false});
            var Q42;
            {var subQ0=sQuery(id+"F3.wireOp",EDGE,"E4");Q42=makeQuery(id+"F5.opExtrude","CAP_EDGE",EDGE,{"disambiguationData":[OSD([subQ0]),TDD([makeQuery(id+"F3.imprint","IMPRINT",EDGE,{"disambiguationData":[TD([[makeQuery(id+"F3.imprint","INTERSECT",VERTEX,{"derivedFrom":[subQ0,sQuery(id+"F3.wireOp",EDGE,"E9.20.3")]}),1.0]])],"derivedFrom":subQ0})])],"isStart":false});}
            var Q43;
            Q43=makeQuery(id+"F5.opExtrude","CAP_EDGE",EDGE,{"disambiguationData":[OSD([sQuery(id+"F3.wireOp",EDGE,"E9.20.0"),sQuery(id+"F3.wireOp",EDGE,"E9.20.1")])],"isStart":false});
            var Q44;
            {var subQ0=sQuery(id+"F3.wireOp",EDGE,"E4");Q44=makeQuery(id+"F5.opExtrude","CAP_EDGE",EDGE,{"disambiguationData":[OSD([subQ0]),TDD([makeQuery(id+"F3.imprint","IMPRINT",EDGE,{"disambiguationData":[TD([[makeQuery(id+"F3.imprint","INTERSECT",VERTEX,{"derivedFrom":[subQ0,sQuery(id+"F3.wireOp",EDGE,"E9.19.3")]}),1.0]])],"derivedFrom":subQ0})])],"isStart":false});}
            var Q45;
            Q45=makeQuery(id+"F5.opExtrude","CAP_EDGE",EDGE,{"disambiguationData":[OSD([sQuery(id+"F3.wireOp",EDGE,"E9.19.0"),sQuery(id+"F3.wireOp",EDGE,"E9.19.1")])],"isStart":false});
            var Q46;
            {var subQ0=sQuery(id+"F3.wireOp",EDGE,"E4");Q46=makeQuery(id+"F5.opExtrude","CAP_EDGE",EDGE,{"disambiguationData":[OSD([subQ0]),TDD([makeQuery(id+"F3.imprint","IMPRINT",EDGE,{"disambiguationData":[TD([[makeQuery(id+"F3.imprint","INTERSECT",VERTEX,{"derivedFrom":[subQ0,sQuery(id+"F3.wireOp",EDGE,"E9.18.3")]}),1.0]])],"derivedFrom":subQ0})])],"isStart":false});}
            var Q47;
            Q47=makeQuery(id+"F5.opExtrude","CAP_EDGE",EDGE,{"disambiguationData":[OSD([sQuery(id+"F3.wireOp",EDGE,"E9.18.0"),sQuery(id+"F3.wireOp",EDGE,"E9.18.1")])],"isStart":false});
            var Q48;
            {var subQ0=sQuery(id+"F3.wireOp",EDGE,"E4");Q48=makeQuery(id+"F5.opExtrude","CAP_EDGE",EDGE,{"disambiguationData":[OSD([subQ0]),TDD([makeQuery(id+"F3.imprint","IMPRINT",EDGE,{"disambiguationData":[TD([[makeQuery(id+"F3.imprint","INTERSECT",VERTEX,{"derivedFrom":[subQ0,sQuery(id+"F3.wireOp",EDGE,"E9.17.3")]}),1.0]])],"derivedFrom":subQ0})])],"isStart":false});}
            var Q49;
            Q49=makeQuery(id+"F5.opExtrude","CAP_EDGE",EDGE,{"disambiguationData":[OSD([sQuery(id+"F3.wireOp",EDGE,"E9.17.0"),sQuery(id+"F3.wireOp",EDGE,"E9.17.1")])],"isStart":false});
            var Q50;
            {var subQ0=sQuery(id+"F3.wireOp",EDGE,"E4");Q50=makeQuery(id+"F5.opExtrude","CAP_EDGE",EDGE,{"disambiguationData":[OSD([subQ0]),TDD([makeQuery(id+"F3.imprint","IMPRINT",EDGE,{"disambiguationData":[TD([[makeQuery(id+"F3.imprint","INTERSECT",VERTEX,{"derivedFrom":[subQ0,sQuery(id+"F3.wireOp",EDGE,"E9.16.3")]}),1.0]])],"derivedFrom":subQ0})])],"isStart":false});}
            var Q51;
            Q51=makeQuery(id+"F5.opExtrude","CAP_EDGE",EDGE,{"disambiguationData":[OSD([sQuery(id+"F3.wireOp",EDGE,"E9.16.0"),sQuery(id+"F3.wireOp",EDGE,"E9.16.1")])],"isStart":false});
            var Q52;
            {var subQ0=sQuery(id+"F3.wireOp",EDGE,"E4");Q52=makeQuery(id+"F5.opExtrude","CAP_EDGE",EDGE,{"disambiguationData":[OSD([subQ0]),TDD([makeQuery(id+"F3.imprint","IMPRINT",EDGE,{"disambiguationData":[TD([[makeQuery(id+"F3.imprint","INTERSECT",VERTEX,{"derivedFrom":[subQ0,sQuery(id+"F3.wireOp",EDGE,"E9.15.3")]}),1.0]])],"derivedFrom":subQ0})])],"isStart":false});}
            var Q53;
            Q53=makeQuery(id+"F5.opExtrude","CAP_EDGE",EDGE,{"disambiguationData":[OSD([sQuery(id+"F3.wireOp",EDGE,"E9.15.0"),sQuery(id+"F3.wireOp",EDGE,"E9.15.1")])],"isStart":false});
            var Q54;
            {var subQ0=sQuery(id+"F3.wireOp",EDGE,"E4");Q54=makeQuery(id+"F5.opExtrude","CAP_EDGE",EDGE,{"disambiguationData":[OSD([subQ0]),TDD([makeQuery(id+"F3.imprint","IMPRINT",EDGE,{"disambiguationData":[TD([[makeQuery(id+"F3.imprint","INTERSECT",VERTEX,{"derivedFrom":[subQ0,sQuery(id+"F3.wireOp",EDGE,"E9.14.3")]}),1.0]])],"derivedFrom":subQ0})])],"isStart":false});}
            var Q55;
            Q55=makeQuery(id+"F5.opExtrude","CAP_EDGE",EDGE,{"disambiguationData":[OSD([sQuery(id+"F3.wireOp",EDGE,"E9.14.0"),sQuery(id+"F3.wireOp",EDGE,"E9.14.1")])],"isStart":false});
            var Q56;
            {var subQ0=sQuery(id+"F3.wireOp",EDGE,"E4");Q56=makeQuery(id+"F5.opExtrude","CAP_EDGE",EDGE,{"disambiguationData":[OSD([subQ0]),TDD([makeQuery(id+"F3.imprint","IMPRINT",EDGE,{"disambiguationData":[TD([[makeQuery(id+"F3.imprint","INTERSECT",VERTEX,{"derivedFrom":[subQ0,sQuery(id+"F3.wireOp",EDGE,"E9.13.3")]}),1.0]])],"derivedFrom":subQ0})])],"isStart":false});}
            var Q57;
            Q57=makeQuery(id+"F5.opExtrude","CAP_EDGE",EDGE,{"disambiguationData":[OSD([sQuery(id+"F3.wireOp",EDGE,"E9.13.0"),sQuery(id+"F3.wireOp",EDGE,"E9.13.1")])],"isStart":false});
            chamfer(context, id + "F7", {"entities" : qUnion([Q0, Q1, Q2, Q3, Q4, Q5, Q6, Q7, Q8, Q9, Q10, Q11, Q12, Q13, Q14, Q15, Q16, Q17, Q18, Q19, Q20, Q21, Q22, Q23, Q24, Q25, Q26, Q27, Q28, Q29, Q30, Q31, Q32, Q33, Q34, Q35, Q36, Q37, Q38, Q39, Q40, Q41, Q42, Q43, Q44, Q45, Q46, Q47, Q48, Q49, Q50, Q51, Q52, Q53, Q54, Q55, Q56, Q57]), "width" : 1 * mm, "tangentPropagation" : true});
        }
        {
            var Q0;
            Q0=qCreatedBy(makeId("Front.planeOp"),FACE);
            var sketch = newSketch(context, id + "F8", { "sketchPlane" : qUnion([Q0])});
            skLineSegment(sketch, "E10", {"start": v(-15, 0) * mm, "end": v(-15, 10) * mm});
            skLineSegment(sketch, "E11.bottom", {"start": v(-15, 0) * mm, "end": v(-17, 0) * mm});
            skLineSegment(sketch, "E11.top", {"start": v(-15, 4) * mm, "end": v(-17, 4) * mm});
            skLineSegment(sketch, "E11.left", {"start": v(-15, 0) * mm, "end": v(-15, 4) * mm});
            skLineSegment(sketch, "E11.right", {"start": v(-17, 0) * mm, "end": v(-17, 4) * mm});
            skLineSegment(sketch, "E12", {"start": v(0, 0) * mm, "end": v(0, -12) * mm});
            skSolve(sketch);
        }
        {
            var Q0;
            Q0=makeQuery(id+"F8.imprint","IMPRINT",FACE,{"disambiguationData":[TD([[makeQuery(id+"F8.imprint","IMPRINT",EDGE,{"derivedFrom":sQuery(id+"F8.wireOp",EDGE,"E11.bottom")}),-1.0]])]});
            var Q1;
            Q1=sQuery(id+"F8.wireOp",EDGE,"E12");
            revolve(context, id + "F9", {"operationType" : NewBodyOperationType.ADD, "entities" : qUnion([Q0]), "axis" : qUnion([Q1]), "revolveType" : RevolveType.FULL});
        }
        {
            var Q0;
            Q0=makeQuery(id+"F9.opRevolve","SWEPT_EDGE",EDGE,{"disambiguationData":[OSD([sQuery(id+"F8.wireOp",EDGE,"E11.top"),sQuery(id+"F8.wireOp",EDGE,"E11.right")])]});
            fillet(context, id + "F10", {"entities" : qUnion([Q0]), "radius" : 0.5 * mm, "tangentPropagation" : true, "allowEdgeOverflow" : false});
        }
    });
